# Revit family: P710058-031-30
name_source: partatom
category: Lighting Fixtures
revit_build: Autodesk Revit 2014 (Build: 20130308_1515(x64)
units: mm (PartAtom-declared; Revit-internal decimal feet)

## types (1)
- P710058-031-30
    Apparent Load = 9 VA
    Assembly Code = D5020200
    Color Filter = 16777215
    Connector Description = Lighting Connector
    Default Elevation = 48 "
    Description = This wall sconce is ideal for corridor and hotel lighting. Circular forms created
a stunning black frame. The light fixture is topped by a summer linen shade
that creates a calming glow sure to welcome tired travelers.
    Diameter = 14 "
    Dimming Lamp Color Temperature Shift = <None>
    Fabric = Paint - Hubbell - White Texture
    Features = • Summer Linen fabric Shade
• This wall sconce is ideal for corridor and hotel lighting.
• Circular forms created a stunning black frame.
• The light fixture is topped by a summer linen shade that creates a calming glow sure to
welcome tired travelers.
• Ideal for any hallway, foyer, living room, sitting room, or bedroom.
• Perfect for mid-century modern, transitional, modern, or contemporary settings.
• Measures 14-inch width by 21-1/4-inch height.
• Uses one LED module (9w max).
• Compatible with many Triac/ELV dimmers (see dimming controls)
• Includes installation instructions and mounting hardware.
• Progress Lighting products are designed for exceptional quality, reliability, and functionality.
• Dimmable to 10% brightness (See Dimming Notes)
• Canopy covers a standard 4” recessed outlet box: 8 in W., 6.5 in ht., 0.812 in depth
• Mounting plate for outlet box included
• 6 in of wire supplied
• Americans With Disabilities Act (ADA) compliant
    Fixture distribution = Direct
    Height = 3.87 "
    Housing Material = Paint - Hubbell - Textured Camera Black
    Lamp = LED
    Load Classification = Lighting
    Manufacturer = Progress Lighting
    Model = P710058-031-30
    Photometric Web File = generic.ies
    Power Factor = 1
    Product Documentation Link = https://hubbellcdn.com
    Product Link = https://www.hubbell.com
    Tilt Angle = -90.00°
    URL = https://www.hubbell.com
    Voltage = 120 V
    Warranty = 5 years Warranty
    Wattage Comments = 9W
    Watts = 9 W

## geometry (parser evidence)
native form markers: Sweep x4
no freeform markers — native parametric forms only
